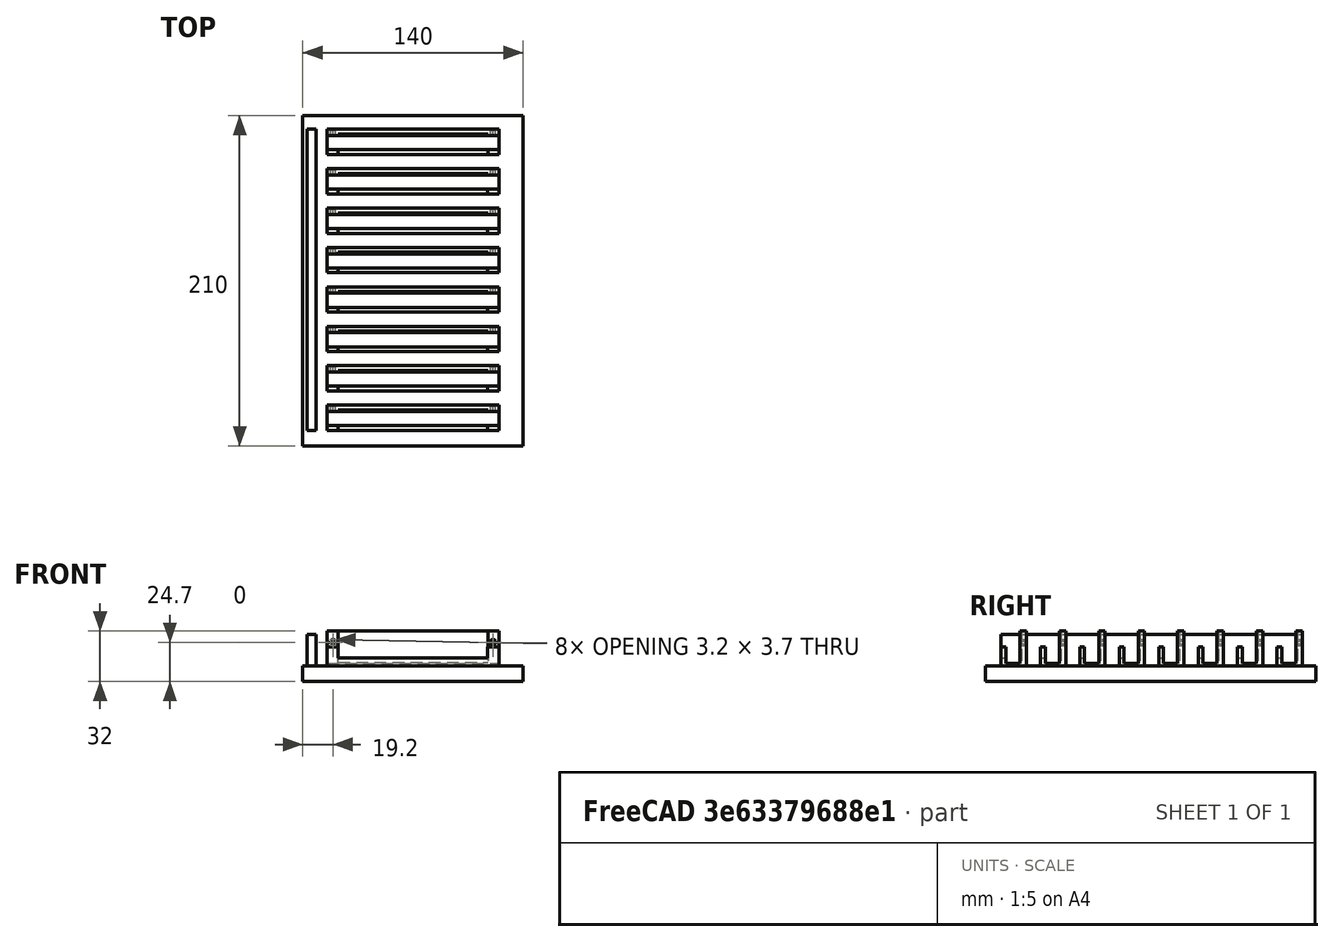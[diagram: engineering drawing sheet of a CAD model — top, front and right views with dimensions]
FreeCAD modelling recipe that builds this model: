
FCSTD DOCUMENT  (FreeCAD 1.0R39109 (Git))
Label: parking
License: All rights reserved
LicenseURL: http://en.wikipedia.org/wiki/All_rights_reserved
objects: Sketcher::SketchObject×20, PartDesign::Pocket×17, PartDesign::Plane×8, Mesh::Feature×6, PartDesign::Pad×3, Spreadsheet::Sheet×1, PartDesign::Body×1
note: 109 computed .brp shape members not serialized (recipe doc carries the construction recipe); baked Part::Feature solids carry a one-line shape summary decoded from their .brp

FEATURE [Sketcher::SketchObject] Sketch
  ArcFitTolerance = 0
  AttachmentSupport = -> [XY_Plane]
  FullyConstrained = true
  MakeInternals = false
  MapMode = 5
  sketch-geometry (4):
    g0: LineSegment StartX=-70 StartY=100 StartZ=0 EndX=70 EndY=100 EndZ=0
    g1: LineSegment StartX=70 StartY=100 StartZ=0 EndX=70 EndY=-110 EndZ=0
    g2: LineSegment StartX=70 StartY=-110 StartZ=0 EndX=-70 EndY=-110 EndZ=0
    g3: LineSegment StartX=-70 StartY=-110 StartZ=0 EndX=-70 EndY=100 EndZ=0
  constraints (11):
    c: Coincident(g0,g1)
    c: Coincident(g1,g2)
    c: Coincident(g2,g3)
    c: Coincident(g3,g0)
    c: Horizontal(g2)
    c: Vertical(g1)
    c: Symmetric(g0,g0,g-2)
    c: DistanceY(g2,g0) = 210
    c: DistanceX(g0,g0) = 140
    c: DistanceY(g-1,g0) = 100
    c: Vertical(g3)
FEATURE [PartDesign::Pad] Pad
  Direction = (0,0,1)
  Length = 12
  Length2 = -2
  Profile = -> Sketch
  ReferenceAxis = -> Sketch [N_Axis]
  Reversed = true
  Suppressed = false
  Type = 4
FEATURE [Spreadsheet::Sheet] Spreadsheet001  label="data001"
  cells = A1='tolerance; B1(tolerance)=0.25; A2='cradle_width; B2(cradle_width)=109.2; A3='cradle_height; B3(cradle_height)=20; A4='cradle_holdermag_sep; B4(cradle_holdermag_sep)=101.6; A5='cradle_holdermag_height; B5(cradle_holdermag_height)=12.7; A6='cradle_thick; B6(cradle_thick)=5; A7='cradlebase_height; B7(cradlebase_height)=7; A8='cradlebase_depth; B8(cradlebase_depth)=20; A9='cradlebase_frontdepth; B9(cradlebase_frontdepth)=10; A10='cradle_holdermag_dim1; B10(cradle_holdermag_dim1)=3; A11='cradle_holdermag_dim2; B11(cradle_holdermag_dim2)=3
FEATURE [Sketcher::SketchObject] Sketch001
  ArcFitTolerance = 0
  AttachmentSupport = -> [YZ_Plane]
  FullyConstrained = true
  MakeInternals = false
  MapMode = 5
  Placement = pos=(0,0,0) rot=(0.57735,0.57735,0.57735;2.0944rad)
  expr: Constraints[10] = <<data001>>.cradle_height
  sketch-geometry (112):
    g0: ArcOfCircle CenterX=-88 CenterY=-6e-16 CenterZ=0 NormalX=0 NormalY=0 NormalZ=1 AngleXU=0 Radius=12 StartAngle=3.14159 EndAngle=4.71239
    g1: LineSegment [constr] StartX=-100 StartY=9e-16 StartZ=0 EndX=-88 EndY=-6e-16 EndZ=0
    g2: LineSegment StartX=-88 StartY=-6e-16 StartZ=0 EndX=-88 EndY=20 EndZ=0
    g3: LineSegment StartX=-88 StartY=20 StartZ=0 EndX=-84 EndY=20 EndZ=0
    g4: LineSegment StartX=-84 StartY=20 StartZ=0 EndX=-84 EndY=-12 EndZ=0
    g5: LineSegment StartX=-88 StartY=-12 StartZ=0 EndX=-84 EndY=-12 EndZ=0
    g6: LineSegment [constr] StartX=-88 StartY=-6e-16 StartZ=0 EndX=-88 EndY=-12 EndZ=0
    g7: LineSegment StartX=-88 StartY=-6e-16 StartZ=0 EndX=-88 EndY=-0.5 EndZ=0
    g8: LineSegment StartX=-88 StartY=-0.5 StartZ=0 EndX=-97 EndY=-0.5 EndZ=0
    g9: LineSegment StartX=-97 StartY=-0.5 StartZ=0 EndX=-97 EndY=0 EndZ=0
    g10: LineSegment StartX=-100 StartY=9e-16 StartZ=0 EndX=-100 EndY=10 EndZ=0
    g11: LineSegment StartX=-100 StartY=10 StartZ=0 EndX=-97 EndY=10 EndZ=0
    g12: LineSegment StartX=-97 StartY=10 StartZ=0 EndX=-97 EndY=0 EndZ=0
    g13: LineSegment [constr] StartX=-100 StartY=10 StartZ=0 EndX=100 EndY=10 EndZ=0
    g14: ArcOfCircle CenterX=-62.9683 CenterY=2e-15 CenterZ=0 NormalX=0 NormalY=0 NormalZ=1 AngleXU=0 Radius=12 StartAngle=3.14159 EndAngle=4.71239
    g15: LineSegment [constr] StartX=-74.9683 StartY=0 StartZ=0 EndX=-62.9683 EndY=2e-15 EndZ=0
    g16: LineSegment StartX=-62.9683 StartY=2e-15 StartZ=0 EndX=-62.9683 EndY=20 EndZ=0
    g17: LineSegment StartX=-62.9683 StartY=20 StartZ=0 EndX=-58.9683 EndY=20 EndZ=0
    g18: LineSegment StartX=-58.9683 StartY=20 StartZ=0 EndX=-58.9683 EndY=-12 EndZ=0
    g19: LineSegment StartX=-62.9683 StartY=-12 StartZ=0 EndX=-58.9683 EndY=-12 EndZ=0
    g20: LineSegment [constr] StartX=-62.9683 StartY=2e-15 StartZ=0 EndX=-62.9683 EndY=-12 EndZ=0
    g21: LineSegment StartX=-62.9683 StartY=2e-15 StartZ=0 EndX=-62.9683 EndY=-0.5 EndZ=0
    g22: LineSegment StartX=-62.9683 StartY=-0.5 StartZ=0 EndX=-71.9683 EndY=-0.5 EndZ=0
    g23: LineSegment StartX=-71.9683 StartY=-0.5 StartZ=0 EndX=-71.9683 EndY=0 EndZ=0
    g24: LineSegment StartX=-74.9683 StartY=0 StartZ=0 EndX=-74.9683 EndY=10 EndZ=0
    g25: LineSegment StartX=-74.9683 StartY=10 StartZ=0 EndX=-71.9683 EndY=10 EndZ=0
    g26: LineSegment StartX=-71.9683 StartY=10 StartZ=0 EndX=-71.9683 EndY=0 EndZ=0
    g27: LineSegment [constr] StartX=-100 StartY=9e-16 StartZ=0 EndX=-74.9683 EndY=0 EndZ=0
    g28: ArcOfCircle CenterX=-37.9367 CenterY=2.1e-15 CenterZ=0 NormalX=0 NormalY=0 NormalZ=1 AngleXU=0 Radius=12 StartAngle=3.14159 EndAngle=4.71239
    g29: LineSegment [constr] StartX=-49.9367 StartY=-1.8e-15 StartZ=0 EndX=-37.9367 EndY=2.1e-15 EndZ=0
    g30: LineSegment StartX=-37.9367 StartY=2.1e-15 StartZ=0 EndX=-37.9367 EndY=20 EndZ=0
    g31: LineSegment StartX=-37.9367 StartY=20 StartZ=0 EndX=-33.9367 EndY=20 EndZ=0
    g32: LineSegment StartX=-33.9367 StartY=20 StartZ=0 EndX=-33.9367 EndY=-12 EndZ=0
    g33: LineSegment StartX=-37.9367 StartY=-12 StartZ=0 EndX=-33.9367 EndY=-12 EndZ=0
    g34: LineSegment [constr] StartX=-37.9367 StartY=2.1e-15 StartZ=0 EndX=-37.9367 EndY=-12 EndZ=0
    g35: LineSegment StartX=-37.9367 StartY=2.1e-15 StartZ=0 EndX=-37.9367 EndY=-0.5 EndZ=0
    g36: LineSegment StartX=-37.9367 StartY=-0.5 StartZ=0 EndX=-46.9367 EndY=-0.5 EndZ=0
    g37: LineSegment StartX=-46.9367 StartY=-0.5 StartZ=0 EndX=-46.9367 EndY=0 EndZ=0
    g38: LineSegment StartX=-49.9367 StartY=-1.8e-15 StartZ=0 EndX=-49.9367 EndY=10 EndZ=0
    g39: LineSegment StartX=-49.9367 StartY=10 StartZ=0 EndX=-46.9367 EndY=10 EndZ=0
    g40: LineSegment StartX=-46.9367 StartY=10 StartZ=0 EndX=-46.9367 EndY=0 EndZ=0
    g41: LineSegment [constr] StartX=-74.9683 StartY=0 StartZ=0 EndX=-49.9367 EndY=-1.8e-15 EndZ=0
    g42: ArcOfCircle CenterX=-12.905 CenterY=2.1e-15 CenterZ=0 NormalX=0 NormalY=0 NormalZ=1 AngleXU=0 Radius=12 StartAngle=3.14159 EndAngle=4.71239
    g43: LineSegment [constr] StartX=-24.905 StartY=-1.8e-15 StartZ=0 EndX=-12.905 EndY=2.1e-15 EndZ=0
    g44: LineSegment StartX=-12.905 StartY=2.1e-15 StartZ=0 EndX=-12.905 EndY=20 EndZ=0
    g45: LineSegment StartX=-12.905 StartY=20 StartZ=0 EndX=-8.90501 EndY=20 EndZ=0
    g46: LineSegment StartX=-8.90501 StartY=20 StartZ=0 EndX=-8.90501 EndY=-12 EndZ=0
    g47: LineSegment StartX=-12.905 StartY=-12 StartZ=0 EndX=-8.90501 EndY=-12 EndZ=0
    g48: LineSegment [constr] StartX=-12.905 StartY=2.1e-15 StartZ=0 EndX=-12.905 EndY=-12 EndZ=0
    g49: LineSegment StartX=-12.905 StartY=2.1e-15 StartZ=0 EndX=-12.905 EndY=-0.5 EndZ=0
    g50: LineSegment StartX=-12.905 StartY=-0.5 StartZ=0 EndX=-21.905 EndY=-0.5 EndZ=0
    g51: LineSegment StartX=-21.905 StartY=-0.5 StartZ=0 EndX=-21.905 EndY=0 EndZ=0
    g52: LineSegment StartX=-24.905 StartY=-1.8e-15 StartZ=0 EndX=-24.905 EndY=10 EndZ=0
    g53: LineSegment StartX=-24.905 StartY=10 StartZ=0 EndX=-21.905 EndY=10 EndZ=0
    g54: LineSegment StartX=-21.905 StartY=10 StartZ=0 EndX=-21.905 EndY=0 EndZ=0
    g55: LineSegment [constr] StartX=-49.9367 StartY=-1.8e-15 StartZ=0 EndX=-24.905 EndY=-1.8e-15 EndZ=0
    g56: ArcOfCircle CenterX=12.1266 CenterY=1.4e-15 CenterZ=0 NormalX=0 NormalY=0 NormalZ=1 AngleXU=0 Radius=12 StartAngle=3.14159 EndAngle=4.71239
    g57: LineSegment [constr] StartX=0.126648 StartY=-2.5e-15 StartZ=0 EndX=12.1266 EndY=1.4e-15 EndZ=0
    g58: LineSegment StartX=12.1266 StartY=1.4e-15 StartZ=0 EndX=12.1266 EndY=20 EndZ=0
    g59: LineSegment StartX=12.1266 StartY=20 StartZ=0 EndX=16.1266 EndY=20 EndZ=0
    g60: LineSegment StartX=16.1266 StartY=20 StartZ=0 EndX=16.1266 EndY=-12 EndZ=0
    g61: LineSegment StartX=12.1266 StartY=-12 StartZ=0 EndX=16.1266 EndY=-12 EndZ=0
    g62: LineSegment [constr] StartX=12.1266 StartY=1.4e-15 StartZ=0 EndX=12.1266 EndY=-12 EndZ=0
    g63: LineSegment StartX=12.1266 StartY=1.4e-15 StartZ=0 EndX=12.1266 EndY=-0.5 EndZ=0
    g64: LineSegment StartX=12.1266 StartY=-0.5 StartZ=0 EndX=3.12665 EndY=-0.5 EndZ=0
    g65: LineSegment StartX=3.12665 StartY=-0.5 StartZ=0 EndX=3.12665 EndY=0 EndZ=0
    g66: LineSegment StartX=0.126648 StartY=-2.5e-15 StartZ=0 EndX=0.126648 EndY=10 EndZ=0
    g67: LineSegment StartX=0.126648 StartY=10 StartZ=0 EndX=3.12665 EndY=10 EndZ=0
    g68: LineSegment StartX=3.12665 StartY=10 StartZ=0 EndX=3.12665 EndY=0 EndZ=0
    g69: LineSegment [constr] StartX=-24.905 StartY=-1.8e-15 StartZ=0 EndX=0.126648 EndY=-2.5e-15 EndZ=0
    g70: ArcOfCircle CenterX=37.1583 CenterY=-2.4e-15 CenterZ=0 NormalX=0 NormalY=0 NormalZ=1 AngleXU=0 Radius=12 StartAngle=3.14159 EndAngle=4.71239
    g71: LineSegment [constr] StartX=25.1583 StartY=0 StartZ=0 EndX=37.1583 EndY=-2.4e-15 EndZ=0
    g72: LineSegment StartX=37.1583 StartY=-2.4e-15 StartZ=0 EndX=37.1583 EndY=20 EndZ=0
    g73: LineSegment StartX=37.1583 StartY=20 StartZ=0 EndX=41.1583 EndY=20 EndZ=0
    g74: LineSegment StartX=41.1583 StartY=20 StartZ=0 EndX=41.1583 EndY=-12 EndZ=0
    g75: LineSegment StartX=37.1583 StartY=-12 StartZ=0 EndX=41.1583 EndY=-12 EndZ=0
    g76: LineSegment [constr] StartX=37.1583 StartY=-2.4e-15 StartZ=0 EndX=37.1583 EndY=-12 EndZ=0
    g77: LineSegment StartX=37.1583 StartY=-2.4e-15 StartZ=0 EndX=37.1583 EndY=-0.5 EndZ=0
    g78: LineSegment StartX=37.1583 StartY=-0.5 StartZ=0 EndX=28.1583 EndY=-0.5 EndZ=0
    g79: LineSegment StartX=28.1583 StartY=-0.5 StartZ=0 EndX=28.1583 EndY=0 EndZ=0
    g80: LineSegment StartX=25.1583 StartY=0 StartZ=0 EndX=25.1583 EndY=10 EndZ=0
    g81: LineSegment StartX=25.1583 StartY=10 StartZ=0 EndX=28.1583 EndY=10 EndZ=0
    g82: LineSegment StartX=28.1583 StartY=10 StartZ=0 EndX=28.1583 EndY=0 EndZ=0
    g83: LineSegment [constr] StartX=0.126648 StartY=-2.5e-15 StartZ=0 EndX=25.1583 EndY=0 EndZ=0
    g84: ArcOfCircle CenterX=62.19 CenterY=1.7e-15 CenterZ=0 NormalX=0 NormalY=0 NormalZ=1 AngleXU=0 Radius=12 StartAngle=3.14159 EndAngle=4.71239
    g85: LineSegment [constr] StartX=50.19 StartY=0 StartZ=0 EndX=62.19 EndY=1.7e-15 EndZ=0
    g86: LineSegment StartX=62.19 StartY=1.7e-15 StartZ=0 EndX=62.19 EndY=20 EndZ=0
    g87: LineSegment StartX=62.19 StartY=20 StartZ=0 EndX=66.19 EndY=20 EndZ=0
    g88: LineSegment StartX=66.19 StartY=20 StartZ=0 EndX=66.19 EndY=-12 EndZ=0
    g89: LineSegment StartX=62.19 StartY=-12 StartZ=0 EndX=66.19 EndY=-12 EndZ=0
    g90: LineSegment [constr] StartX=62.19 StartY=1.7e-15 StartZ=0 EndX=62.19 EndY=-12 EndZ=0
    g91: LineSegment StartX=62.19 StartY=1.7e-15 StartZ=0 EndX=62.19 EndY=-0.5 EndZ=0
    g92: LineSegment StartX=62.19 StartY=-0.5 StartZ=0 EndX=53.19 EndY=-0.5 EndZ=0
    g93: LineSegment StartX=53.19 StartY=-0.5 StartZ=0 EndX=53.19 EndY=0 EndZ=0
    g94: LineSegment StartX=50.19 StartY=0 StartZ=0 EndX=50.19 EndY=10 EndZ=0
    g95: LineSegment StartX=50.19 StartY=10 StartZ=0 EndX=53.19 EndY=10 EndZ=0
    g96: LineSegment StartX=53.19 StartY=10 StartZ=0 EndX=53.19 EndY=0 EndZ=0
    g97: LineSegment [constr] StartX=25.1583 StartY=0 StartZ=0 EndX=50.19 EndY=0 EndZ=0
    g98: ArcOfCircle CenterX=87.2216 CenterY=-6e-16 CenterZ=0 NormalX=0 NormalY=0 NormalZ=1 AngleXU=0 Radius=12 StartAngle=3.14159 EndAngle=4.71239
    g99: LineSegment [constr] StartX=75.2216 StartY=0 StartZ=0 EndX=87.2216 EndY=-6e-16 EndZ=0
    g100: LineSegment StartX=87.2216 StartY=-6e-16 StartZ=0 EndX=87.2216 EndY=20 EndZ=0
    g101: LineSegment StartX=87.2216 StartY=20 StartZ=0 EndX=91.2216 EndY=20 EndZ=0
    g102: LineSegment StartX=91.2216 StartY=20 StartZ=0 EndX=91.2216 EndY=-12 EndZ=0
    g103: LineSegment StartX=87.2216 StartY=-12 StartZ=0 EndX=91.2216 EndY=-12 EndZ=0
    g104: LineSegment [constr] StartX=87.2216 StartY=-6e-16 StartZ=0 EndX=87.2216 EndY=-12 EndZ=0
    g105: LineSegment StartX=87.2216 StartY=-6e-16 StartZ=0 EndX=87.2216 EndY=-0.5 EndZ=0
    g106: LineSegment StartX=87.2216 StartY=-0.5 StartZ=0 EndX=78.2216 EndY=-0.5 EndZ=0
    g107: LineSegment StartX=78.2216 StartY=-0.5 StartZ=0 EndX=78.2216 EndY=0 EndZ=0
    g108: LineSegment StartX=75.2216 StartY=0 StartZ=0 EndX=75.2216 EndY=10 EndZ=0
    g109: LineSegment StartX=75.2216 StartY=10 StartZ=0 EndX=78.2216 EndY=10 EndZ=0
    g110: LineSegment StartX=78.2216 StartY=10 StartZ=0 EndX=78.2216 EndY=0 EndZ=0
    g111: LineSegment [constr] StartX=50.19 StartY=0 StartZ=0 EndX=75.2216 EndY=0 EndZ=0
  constraints (313):
    c: Radius(g0) = 12
    c: Coincident(g1,g0)
    c: Coincident(g1,g0)
    c: Coincident(g2,g0)
    c: Coincident(g3,g2)
    c: Horizontal(g3)
    c: Coincident(g5,g0)
    c: Coincident(g5,g4)
    c: Horizontal(g5)
    c: Vertical(g4)
    c: Distance(g2,g0) = 20
    c: Coincident(g4,g3)
    c: Coincident(g6,g0)
    c: Coincident(g6,g0)
    c: Angle(g1,g6) = 1.5708
    c: Angle(g2,g1) = 1.5708
    c: DistanceX(g2,g3) = 4
    c: Coincident(g7,g0)
    c: PointOnObject(g7,g6)
    c: Coincident(g8,g7)
    c: Coincident(g9,g8)
    c: PointOnObject(g9,g1)
    c: Distance(g7,g0) = 0.5
    c: Parallel(g9,g6)
    c: Parallel(g8,g1)
    c: Distance(g8,g7) = 9
    c: Coincident(g10,g0)
    c: Coincident(g11,g10)
    c: Coincident(g12,g11)
    c: Coincident(g12,g9)
    c: Parallel(g10,g2)
    c: Parallel(g6,g4)
    c: Parallel(g10,g12)
    c: Parallel(g11,g1)
    c: PointOnObject(g0,g-1)
    c: Distance(g10) = 10
    c: Distance(g0,g-1) = 100
    c: Coincident(g13,g10)
    c: Horizontal(g13)
    c: DistanceX(g13,g13) = 200
    c: Equal(g0,g14) = 12
    c: Coincident(g15,g14)
    c: Coincident(g15,g14)
    c: Coincident(g16,g14)
    c: Coincident(g17,g16)
    c: Horizontal(g17)
    c: Coincident(g19,g14)
    c: Coincident(g19,g18)
    c: Horizontal(g19)
    c: Vertical(g18)
    c: Distance(g16,g14) = 20
    c: Coincident(g18,g17)
    c: Coincident(g20,g14)
    c: Coincident(g20,g14)
    c: Angle(g15,g20) = 1.5708
    c: Angle(g16,g15) = 1.5708
    c: DistanceX(g16,g17) = 4
    c: Coincident(g21,g14)
    c: PointOnObject(g21,g20)
    c: Coincident(g22,g21)
    c: Coincident(g23,g22)
    c: PointOnObject(g23,g15)
    c: Distance(g21,g14) = 0.5
    c: Parallel(g23,g20)
    c: Parallel(g22,g15)
    c: Distance(g22,g21) = 9
    c: Coincident(g24,g14)
    c: Coincident(g25,g24)
    c: Coincident(g26,g25)
    c: Coincident(g26,g23)
    c: Parallel(g24,g16)
    c: Parallel(g20,g18)
    c: Parallel(g24,g26)
    c: Parallel(g25,g15)
    c: Equal(g10,g24) = 10
    c: Coincident(g0,g27)
    c: Coincident(g14,g27)
    c: Distance(g27) = 25.0317
    c: Angle(g27) = 0
    c: Equal(g0,g28) = 12
    c: Coincident(g29,g28)
    c: Coincident(g29,g28)
    c: Coincident(g30,g28)
    c: Coincident(g31,g30)
    c: Horizontal(g31)
    c: Coincident(g33,g28)
    c: Coincident(g33,g32)
    c: Horizontal(g33)
    c: Vertical(g32)
    c: Distance(g30,g28) = 20
    c: Coincident(g32,g31)
    c: Coincident(g34,g28)
    c: Coincident(g34,g28)
    c: Angle(g29,g34) = 1.5708
    c: Angle(g30,g29) = 1.5708
    c: DistanceX(g30,g31) = 4
    c: Coincident(g35,g28)
    c: PointOnObject(g35,g34)
    c: Coincident(g36,g35)
    c: Coincident(g37,g36)
    c: PointOnObject(g37,g29)
    c: Distance(g35,g28) = 0.5
    c: Parallel(g37,g34)
    c: Parallel(g36,g29)
    c: Distance(g36,g35) = 9
    c: Coincident(g38,g28)
    c: Coincident(g39,g38)
    c: Coincident(g40,g39)
    c: Coincident(g40,g37)
    c: Parallel(g38,g30)
    c: Parallel(g34,g32)
    c: Parallel(g38,g40)
    c: Parallel(g39,g29)
    c: Equal(g10,g38) = 10
    c: Coincident(g14,g41)
    c: Coincident(g28,g41)
    c: Equal(g27,g41)
    c: Parallel(g41,g27)
    c: Equal(g0,g42) = 12
    c: Coincident(g43,g42)
    c: Coincident(g43,g42)
    c: Coincident(g44,g42)
    c: Coincident(g45,g44)
    c: Horizontal(g45)
    c: Coincident(g47,g42)
    c: Coincident(g47,g46)
    c: Horizontal(g47)
    c: Vertical(g46)
    c: Distance(g44,g42) = 20
    c: Coincident(g46,g45)
    c: Coincident(g48,g42)
    c: Coincident(g48,g42)
    c: Angle(g43,g48) = 1.5708
    c: Angle(g44,g43) = 1.5708
    c: DistanceX(g44,g45) = 4
    c: Coincident(g49,g42)
    c: PointOnObject(g49,g48)
    c: Coincident(g50,g49)
    c: Coincident(g51,g50)
    c: PointOnObject(g51,g43)
    c: Distance(g49,g42) = 0.5
    c: Parallel(g51,g48)
    c: Parallel(g50,g43)
    c: Distance(g50,g49) = 9
    c: Coincident(g52,g42)
    c: Coincident(g53,g52)
    c: Coincident(g54,g53)
    c: Coincident(g54,g51)
    c: Parallel(g52,g44)
    c: Parallel(g48,g46)
    c: Parallel(g52,g54)
    c: Parallel(g53,g43)
    c: Equal(g10,g52) = 10
    c: Coincident(g28,g55)
    c: Coincident(g42,g55)
    c: Equal(g27,g55)
    c: Parallel(g55,g27)
    c: Equal(g0,g56) = 12
    c: Coincident(g57,g56)
    c: Coincident(g57,g56)
    c: Coincident(g58,g56)
    c: Coincident(g59,g58)
    c: Horizontal(g59)
    c: Coincident(g61,g56)
    c: Coincident(g61,g60)
    c: Horizontal(g61)
    c: Vertical(g60)
    c: Distance(g58,g56) = 20
    c: Coincident(g60,g59)
    c: Coincident(g62,g56)
    c: Coincident(g62,g56)
    c: Angle(g57,g62) = 1.5708
    c: Angle(g58,g57) = 1.5708
    c: DistanceX(g58,g59) = 4
    c: Coincident(g63,g56)
    c: PointOnObject(g63,g62)
    c: Coincident(g64,g63)
    c: Coincident(g65,g64)
    c: PointOnObject(g65,g57)
    c: Distance(g63,g56) = 0.5
    c: Parallel(g65,g62)
    c: Parallel(g64,g57)
    c: Distance(g64,g63) = 9
    c: Coincident(g66,g56)
    c: Coincident(g67,g66)
    c: Coincident(g68,g67)
    c: Coincident(g68,g65)
    c: Parallel(g66,g58)
    c: Parallel(g62,g60)
    c: Parallel(g66,g68)
    c: Parallel(g67,g57)
    c: Equal(g10,g66) = 10
    c: Coincident(g42,g69)
    c: Coincident(g56,g69)
    c: Equal(g27,g69)
    c: Parallel(g69,g27)
    c: Equal(g0,g70) = 12
    c: Coincident(g71,g70)
    c: Coincident(g71,g70)
    c: Coincident(g72,g70)
    c: Coincident(g73,g72)
    c: Horizontal(g73)
    c: Coincident(g75,g70)
    c: Coincident(g75,g74)
    c: Horizontal(g75)
    c: Vertical(g74)
    c: Distance(g72,g70) = 20
    c: Coincident(g74,g73)
    c: Coincident(g76,g70)
    c: Coincident(g76,g70)
    c: Angle(g71,g76) = 1.5708
    c: Angle(g72,g71) = 1.5708
    c: DistanceX(g72,g73) = 4
    c: Coincident(g77,g70)
    c: PointOnObject(g77,g76)
    c: Coincident(g78,g77)
    c: Coincident(g79,g78)
    c: PointOnObject(g79,g71)
    c: Distance(g77,g70) = 0.5
    c: Parallel(g79,g76)
    c: Parallel(g78,g71)
    c: Distance(g78,g77) = 9
    c: Coincident(g80,g70)
    c: Coincident(g81,g80)
    c: Coincident(g82,g81)
    c: Coincident(g82,g79)
    c: Parallel(g80,g72)
    c: Parallel(g76,g74)
    c: Parallel(g80,g82)
    c: Parallel(g81,g71)
    c: Equal(g10,g80) = 10
    c: Coincident(g56,g83)
    c: Coincident(g70,g83)
    c: Equal(g27,g83)
    c: Parallel(g83,g27)
    c: Equal(g0,g84) = 12
    c: Coincident(g85,g84)
    c: Coincident(g85,g84)
    c: Coincident(g86,g84)
    c: Coincident(g87,g86)
    c: Horizontal(g87)
    c: Coincident(g89,g84)
    c: Coincident(g89,g88)
    c: Horizontal(g89)
    c: Vertical(g88)
    c: Distance(g86,g84) = 20
    c: Coincident(g88,g87)
    c: Coincident(g90,g84)
    c: Coincident(g90,g84)
    c: Angle(g85,g90) = 1.5708
    c: Angle(g86,g85) = 1.5708
    c: DistanceX(g86,g87) = 4
    c: Coincident(g91,g84)
    c: PointOnObject(g91,g90)
    c: Coincident(g92,g91)
    c: Coincident(g93,g92)
    c: PointOnObject(g93,g85)
    c: Distance(g91,g84) = 0.5
    c: Parallel(g93,g90)
    c: Parallel(g92,g85)
    c: Distance(g92,g91) = 9
    c: Coincident(g94,g84)
    c: Coincident(g95,g94)
    c: Coincident(g96,g95)
    c: Coincident(g96,g93)
    c: Parallel(g94,g86)
    c: Parallel(g90,g88)
    c: Parallel(g94,g96)
    c: Parallel(g95,g85)
    c: Equal(g10,g94) = 10
    c: Coincident(g70,g97)
    c: Coincident(g84,g97)
    c: Equal(g27,g97)
    c: Parallel(g97,g27)
    c: Equal(g0,g98) = 12
    c: Coincident(g99,g98)
    c: Coincident(g99,g98)
    c: Coincident(g100,g98)
    c: Coincident(g101,g100)
    c: Horizontal(g101)
    c: Coincident(g103,g98)
    c: Coincident(g103,g102)
    c: Horizontal(g103)
    c: Vertical(g102)
    c: Distance(g100,g98) = 20
    c: Coincident(g102,g101)
    c: Coincident(g104,g98)
    c: Coincident(g104,g98)
    c: Angle(g99,g104) = 1.5708
    c: Angle(g100,g99) = 1.5708
    c: DistanceX(g100,g101) = 4
    c: Coincident(g105,g98)
    c: PointOnObject(g105,g104)
    c: Coincident(g106,g105)
    c: Coincident(g107,g106)
    c: PointOnObject(g107,g99)
    c: Distance(g105,g98) = 0.5
    c: Parallel(g107,g104)
    c: Parallel(g106,g99)
    c: Distance(g106,g105) = 9
    c: Coincident(g108,g98)
    c: Coincident(g109,g108)
    c: Coincident(g110,g109)
    c: Coincident(g110,g107)
    c: Parallel(g108,g100)
    c: Parallel(g104,g102)
    c: Parallel(g108,g110)
    c: Parallel(g109,g99)
    c: Equal(g10,g108) = 10
    c: Coincident(g84,g111)
    c: Coincident(g98,g111)
    c: Equal(g27,g111)
    c: Parallel(g111,g27)
FEATURE [PartDesign::Pad] Pad001
  BaseFeature = -> Pad
  Direction = (1,0,0)
  Length = 109.2
  Length2 = 10
  Midplane = true
  Profile = -> Sketch001
  ReferenceAxis = -> Sketch001 [N_Axis]
  Suppressed = false
  Type = 0
  expr: Length = <<data001>>.cradle_width
FEATURE [Mesh::Feature] Mesh  label="20 degrees"
FEATURE [Mesh::Feature] Mesh001  label="30 degrees"
FEATURE [Mesh::Feature] Mesh002  label="5 degrees"
FEATURE [Mesh::Feature] Mesh003  label="0 degrees"
FEATURE [Mesh::Feature] Mesh004  label="Pocket008 (Meshed)"
FEATURE [Sketcher::SketchObject] Sketch002
  ArcFitTolerance = 0
  AttachmentSupport = -> [Pad001]
  FullyConstrained = false
  MakeInternals = false
  MapMode = 5
  Placement = pos=(0,0,-2) rot=(0,0,1;0rad)
  sketch-geometry (4):
    g0: LineSegment StartX=-67.1563 StartY=-100.063 StartZ=0 EndX=-61.6543 EndY=-100.063 EndZ=0
    g1: LineSegment StartX=-61.6543 StartY=-100.063 StartZ=0 EndX=-61.6543 EndY=91.28 EndZ=0
    g2: LineSegment StartX=-61.6543 StartY=91.28 StartZ=0 EndX=-67.1563 EndY=91.28 EndZ=0
    g3: LineSegment StartX=-67.1563 StartY=91.28 StartZ=0 EndX=-67.1563 EndY=-100.063 EndZ=0
  constraints (8):
    c: Coincident(g0,g1)
    c: Coincident(g1,g2)
    c: Coincident(g2,g3)
    c: Coincident(g3,g0)
    c: Horizontal(g0)
    c: Horizontal(g2)
    c: Vertical(g1)
    c: Vertical(g3)
FEATURE [PartDesign::Pad] Pad002
  BaseFeature = -> Pad001
  Direction = (0,0,1)
  Length = 20
  Length2 = 10
  Profile = -> Sketch002
  ReferenceAxis = -> Sketch002 [N_Axis]
  Suppressed = false
  Type = 0
FEATURE [PartDesign::Plane] DatumPlane
  AttachmentSupport = -> [Pad002]
  Length = 156.733
  MapMode = 5
  Placement = pos=(0,-88,0) rot=(1,0,0;1.5708rad)
  ResizeMode = 0
  Width = 66.7332
FEATURE [Sketcher::SketchObject] Sketch004
  ArcFitTolerance = 0
  AttachmentSupport = -> [DatumPlane]
  FullyConstrained = true
  MakeInternals = false
  MapMode = 5
  Placement = pos=(0,-88,0) rot=(1,0,0;1.5708rad)
  expr: Constraints[38] = <<data001>>.cradle_holdermag_sep
  sketch-geometry (14):
    g0: LineSegment StartX=-49.1979 StartY=11.775 StartZ=0 EndX=-49.1979 EndY=13.625 EndZ=0
    g1: LineSegment StartX=-49.1979 StartY=13.625 StartZ=0 EndX=-50.8 EndY=14.55 EndZ=0
    g2: LineSegment StartX=-50.8 StartY=14.55 StartZ=0 EndX=-52.4021 EndY=13.625 EndZ=0
    g3: LineSegment StartX=-52.4021 StartY=13.625 StartZ=0 EndX=-52.4021 EndY=11.775 EndZ=0
    g4: LineSegment StartX=-52.4021 StartY=11.775 StartZ=0 EndX=-50.8 EndY=10.85 EndZ=0
    g5: LineSegment StartX=-50.8 StartY=10.85 StartZ=0 EndX=-49.1979 EndY=11.775 EndZ=0
    g6: Circle [constr] CenterX=-50.8 CenterY=12.7 CenterZ=0 NormalX=0 NormalY=0 NormalZ=1 AngleXU=0 Radius=1.85
    g7: LineSegment StartX=52.4021 StartY=11.775 StartZ=0 EndX=52.4021 EndY=13.625 EndZ=0
    g8: LineSegment StartX=52.4021 StartY=13.625 StartZ=0 EndX=50.8 EndY=14.55 EndZ=0
    g9: LineSegment StartX=50.8 StartY=14.55 StartZ=0 EndX=49.1979 EndY=13.625 EndZ=0
    g10: LineSegment StartX=49.1979 StartY=13.625 StartZ=0 EndX=49.1979 EndY=11.775 EndZ=0
    g11: LineSegment StartX=49.1979 StartY=11.775 StartZ=0 EndX=50.8 EndY=10.85 EndZ=0
    g12: LineSegment StartX=50.8 StartY=10.85 StartZ=0 EndX=52.4021 EndY=11.775 EndZ=0
    g13: Circle [constr] CenterX=50.8 CenterY=12.7 CenterZ=0 NormalX=0 NormalY=0 NormalZ=1 AngleXU=0 Radius=1.85
  constraints (33):
    c: Coincident(g0,g1)
    c: Coincident(g1,g2)
    c: Coincident(g2,g3)
    c: Coincident(g3,g4)
    c: Coincident(g4,g5)
    c: Coincident(g5,g0)
    c: Equal(g0, g1-g5) x5
    c: PointOnObject(g0,g6)
    c: PointOnObject(g1,g6)
    c: PointOnObject(g2,g6)
    c: PointOnObject(g3,g6)
    c: PointOnObject(g4,g6)
    c: PointOnObject(g5,g6)
    c: Coincident(g7,g8)
    c: Coincident(g8,g9)
    c: Coincident(g9,g10)
    c: Coincident(g10,g11)
    c: Coincident(g11,g12)
    c: Coincident(g12,g7)
    c: Equal(g7, g8-g12) x5
    c: PointOnObject(g7,g13)
    c: PointOnObject(g8,g13)
    c: PointOnObject(g9,g13)
    c: PointOnObject(g10,g13)
    c: PointOnObject(g11,g13)
    c: PointOnObject(g12,g13)
    c: Parallel(g0,g-2)
    c: Equal(g2,g10)
    c: Parallel(g10,g-2)
    c: Symmetric(g6,g13,g-2)
    c: DistanceX(g6,g13) = 101.6
    c: DistanceY(g-1,g6) = 12.7
    c: Radius(g6) = 1.85
FEATURE [Sketcher::SketchObject] Sketch005
  ArcFitTolerance = 0
  AttachmentSupport = -> [DatumPlane]
  FullyConstrained = true
  MakeInternals = false
  MapMode = 5
  Placement = pos=(0,-88,0) rot=(1,0,0;1.5708rad)
  sketch-geometry (4):
    g0: LineSegment StartX=-47.5 StartY=22 StartZ=0 EndX=47.5 EndY=22 EndZ=0
    g1: LineSegment StartX=47.5 StartY=22 StartZ=0 EndX=47.5 EndY=0 EndZ=0
    g2: LineSegment StartX=47.5 StartY=0 StartZ=0 EndX=-47.5 EndY=0 EndZ=0
    g3: LineSegment StartX=-47.5 StartY=0 StartZ=0 EndX=-47.5 EndY=22 EndZ=0
  constraints (11):
    c: Coincident(g0,g1)
    c: Coincident(g1,g2)
    c: Coincident(g2,g3)
    c: Coincident(g3,g0)
    c: Horizontal(g2)
    c: Vertical(g1)
    c: Vertical(g3)
    c: PointOnObject(g1,g-1)
    c: DistanceY(g2,g0) = 22
    c: DistanceX(g0,g0) = 95
    c: Symmetric(g0,g0,g-2)
FEATURE [PartDesign::Plane] DatumPlane001 .. DatumPlane007  x7 (patterned run collapsed; names and placements below)
  AttachmentSupport = -> [Pad002]
  Length = 156.733
  MapMode = 5
  ResizeMode = 0
  Width = 66.7332
  placements: 7 in arithmetic series — first pos=(0,-62.9683,2.24e-14) rot=(1,0,0;1.5708rad), step (0,25.0317,-3.59e-14), last pos=(0,87.2216,0) rot=(1,0,0;1.5708rad)
FEATURE [PartDesign::Pocket] Pocket
  BaseFeature = -> Pad002
  Direction = (0,1,-2e-16)
  Length = 3.5
  Length2 = 5
  Profile = -> Sketch004
  ReferenceAxis = -> Sketch004 [N_Axis]
  Suppressed = false
  Type = 0
FEATURE [PartDesign::Pocket] Pocket001
  BaseFeature = -> Pocket
  Direction = (0,1,-2e-16)
  Length = 1
  Length2 = 5
  Profile = -> Sketch005
  ReferenceAxis = -> Sketch005 [N_Axis]
  Suppressed = false
  Type = 0
FEATURE [Sketcher::SketchObject] Sketch006
  ArcFitTolerance = 0
  AttachmentSupport = -> [DatumPlane001]
  FullyConstrained = true
  MakeInternals = false
  MapMode = 5
  Placement = pos=(0,-62.9683,2.24e-14) rot=(1,0,0;1.5708rad)
  expr: Constraints[38] = Sketch004.Constraints[38]
  expr: Constraints[39] = Sketch004.Constraints[39]
  expr: Constraints[40] = Sketch004.Constraints[40]
  sketch-geometry (14):
    g0: LineSegment StartX=-49.1979 StartY=11.775 StartZ=0 EndX=-49.1979 EndY=13.625 EndZ=0
    g1: LineSegment StartX=-49.1979 StartY=13.625 StartZ=0 EndX=-50.8 EndY=14.55 EndZ=0
    g2: LineSegment StartX=-50.8 StartY=14.55 StartZ=0 EndX=-52.4021 EndY=13.625 EndZ=0
    g3: LineSegment StartX=-52.4021 StartY=13.625 StartZ=0 EndX=-52.4021 EndY=11.775 EndZ=0
    g4: LineSegment StartX=-52.4021 StartY=11.775 StartZ=0 EndX=-50.8 EndY=10.85 EndZ=0
    g5: LineSegment StartX=-50.8 StartY=10.85 StartZ=0 EndX=-49.1979 EndY=11.775 EndZ=0
    g6: Circle [constr] CenterX=-50.8 CenterY=12.7 CenterZ=0 NormalX=0 NormalY=0 NormalZ=1 AngleXU=0 Radius=1.85
    g7: LineSegment StartX=52.4021 StartY=11.775 StartZ=0 EndX=52.4021 EndY=13.625 EndZ=0
    g8: LineSegment StartX=52.4021 StartY=13.625 StartZ=0 EndX=50.8 EndY=14.55 EndZ=0
    g9: LineSegment StartX=50.8 StartY=14.55 StartZ=0 EndX=49.1979 EndY=13.625 EndZ=0
    g10: LineSegment StartX=49.1979 StartY=13.625 StartZ=0 EndX=49.1979 EndY=11.775 EndZ=0
    g11: LineSegment StartX=49.1979 StartY=11.775 StartZ=0 EndX=50.8 EndY=10.85 EndZ=0
    g12: LineSegment StartX=50.8 StartY=10.85 StartZ=0 EndX=52.4021 EndY=11.775 EndZ=0
    g13: Circle [constr] CenterX=50.8 CenterY=12.7 CenterZ=0 NormalX=0 NormalY=0 NormalZ=1 AngleXU=0 Radius=1.85
  constraints (33):
    c: Coincident(g0,g1)
    c: Coincident(g1,g2)
    c: Coincident(g2,g3)
    c: Coincident(g3,g4)
    c: Coincident(g4,g5)
    c: Coincident(g5,g0)
    c: Equal(g0, g1-g5) x5
    c: PointOnObject(g0,g6)
    c: PointOnObject(g1,g6)
    c: PointOnObject(g2,g6)
    c: PointOnObject(g3,g6)
    c: PointOnObject(g4,g6)
    c: PointOnObject(g5,g6)
    c: Coincident(g7,g8)
    c: Coincident(g8,g9)
    c: Coincident(g9,g10)
    c: Coincident(g10,g11)
    c: Coincident(g11,g12)
    c: Coincident(g12,g7)
    c: Equal(g7, g8-g12) x5
    c: PointOnObject(g7,g13)
    c: PointOnObject(g8,g13)
    c: PointOnObject(g9,g13)
    c: PointOnObject(g10,g13)
    c: PointOnObject(g11,g13)
    c: PointOnObject(g12,g13)
    c: Parallel(g0,g-2)
    c: Equal(g2,g10)
    c: Parallel(g10,g-2)
    c: Symmetric(g6,g13,g-2)
    c: DistanceX(g6,g13) = 101.6
    c: DistanceY(g-1,g6) = 12.7
    c: Radius(g6) = 1.85
FEATURE [PartDesign::Pocket] Pocket002
  BaseFeature = -> Pocket001
  Direction = (0,1,-2e-16)
  Length = 3.5
  Length2 = 5
  Profile = -> Sketch006
  ReferenceAxis = -> Sketch006 [N_Axis]
  Suppressed = false
  Type = 0
FEATURE [Sketcher::SketchObject] Sketch007
  ArcFitTolerance = 0
  AttachmentSupport = -> [DatumPlane001]
  FullyConstrained = true
  MakeInternals = false
  MapMode = 5
  Placement = pos=(0,-62.9683,2.24e-14) rot=(1,0,0;1.5708rad)
  expr: Constraints[8] = Sketch005.Constraints[8]
  expr: Constraints[9] = Sketch005.Constraints[9]
  sketch-geometry (4):
    g0: LineSegment StartX=-47.5 StartY=22 StartZ=0 EndX=47.5 EndY=22 EndZ=0
    g1: LineSegment StartX=47.5 StartY=22 StartZ=0 EndX=47.5 EndY=0 EndZ=0
    g2: LineSegment StartX=47.5 StartY=0 StartZ=0 EndX=-47.5 EndY=0 EndZ=0
    g3: LineSegment StartX=-47.5 StartY=0 StartZ=0 EndX=-47.5 EndY=22 EndZ=0
  constraints (11):
    c: Coincident(g0,g1)
    c: Coincident(g1,g2)
    c: Coincident(g2,g3)
    c: Coincident(g3,g0)
    c: Horizontal(g2)
    c: Vertical(g1)
    c: Vertical(g3)
    c: PointOnObject(g1,g-1)
    c: DistanceY(g2,g0) = 22
    c: DistanceX(g0,g0) = 95
    c: Symmetric(g0,g0,g-2)
FEATURE [PartDesign::Pocket] Pocket003
  BaseFeature = -> Pocket002
  Direction = (0,1,-2e-16)
  Length = 1
  Length2 = 5
  Profile = -> Sketch007
  ReferenceAxis = -> Sketch007 [N_Axis]
  Suppressed = false
  Type = 0
FEATURE [Sketcher::SketchObject] Sketch008
  ArcFitTolerance = 0
  AttachmentSupport = -> [DatumPlane002]
  FullyConstrained = true
  MakeInternals = false
  MapMode = 5
  Placement = pos=(0,-37.9367,-1.35e-14) rot=(1,0,0;1.5708rad)
  expr: Constraints[38] = Sketch004.Constraints[38]
  expr: Constraints[39] = Sketch004.Constraints[39]
  expr: Constraints[40] = Sketch004.Constraints[40]
  sketch-geometry (14):
    g0: LineSegment StartX=-49.1979 StartY=11.775 StartZ=0 EndX=-49.1979 EndY=13.625 EndZ=0
    g1: LineSegment StartX=-49.1979 StartY=13.625 StartZ=0 EndX=-50.8 EndY=14.55 EndZ=0
    g2: LineSegment StartX=-50.8 StartY=14.55 StartZ=0 EndX=-52.4021 EndY=13.625 EndZ=0
    g3: LineSegment StartX=-52.4021 StartY=13.625 StartZ=0 EndX=-52.4021 EndY=11.775 EndZ=0
    g4: LineSegment StartX=-52.4021 StartY=11.775 StartZ=0 EndX=-50.8 EndY=10.85 EndZ=0
    g5: LineSegment StartX=-50.8 StartY=10.85 StartZ=0 EndX=-49.1979 EndY=11.775 EndZ=0
    g6: Circle [constr] CenterX=-50.8 CenterY=12.7 CenterZ=0 NormalX=0 NormalY=0 NormalZ=1 AngleXU=0 Radius=1.85
    g7: LineSegment StartX=52.4021 StartY=11.775 StartZ=0 EndX=52.4021 EndY=13.625 EndZ=0
    g8: LineSegment StartX=52.4021 StartY=13.625 StartZ=0 EndX=50.8 EndY=14.55 EndZ=0
    g9: LineSegment StartX=50.8 StartY=14.55 StartZ=0 EndX=49.1979 EndY=13.625 EndZ=0
    g10: LineSegment StartX=49.1979 StartY=13.625 StartZ=0 EndX=49.1979 EndY=11.775 EndZ=0
    g11: LineSegment StartX=49.1979 StartY=11.775 StartZ=0 EndX=50.8 EndY=10.85 EndZ=0
    g12: LineSegment StartX=50.8 StartY=10.85 StartZ=0 EndX=52.4021 EndY=11.775 EndZ=0
    g13: Circle [constr] CenterX=50.8 CenterY=12.7 CenterZ=0 NormalX=0 NormalY=0 NormalZ=1 AngleXU=0 Radius=1.85
  constraints (33):
    c: Coincident(g0,g1)
    c: Coincident(g1,g2)
    c: Coincident(g2,g3)
    c: Coincident(g3,g4)
    c: Coincident(g4,g5)
    c: Coincident(g5,g0)
    c: Equal(g0, g1-g5) x5
    c: PointOnObject(g0,g6)
    c: PointOnObject(g1,g6)
    c: PointOnObject(g2,g6)
    c: PointOnObject(g3,g6)
    c: PointOnObject(g4,g6)
    c: PointOnObject(g5,g6)
    c: Coincident(g7,g8)
    c: Coincident(g8,g9)
    c: Coincident(g9,g10)
    c: Coincident(g10,g11)
    c: Coincident(g11,g12)
    c: Coincident(g12,g7)
    c: Equal(g7, g8-g12) x5
    c: PointOnObject(g7,g13)
    c: PointOnObject(g8,g13)
    c: PointOnObject(g9,g13)
    c: PointOnObject(g10,g13)
    c: PointOnObject(g11,g13)
    c: PointOnObject(g12,g13)
    c: Parallel(g0,g-2)
    c: Equal(g2,g10)
    c: Parallel(g10,g-2)
    c: Symmetric(g6,g13,g-2)
    c: DistanceX(g6,g13) = 101.6
    c: DistanceY(g-1,g6) = 12.7
    c: Radius(g6) = 1.85
FEATURE [PartDesign::Pocket] Pocket004
  BaseFeature = -> Pocket003
  Direction = (0,1,-2e-16)
  Length = 3.5
  Length2 = 5
  Profile = -> Sketch008
  ReferenceAxis = -> Sketch008 [N_Axis]
  Suppressed = false
  Type = 0
FEATURE [Sketcher::SketchObject] Sketch009
  ArcFitTolerance = 0
  AttachmentSupport = -> [DatumPlane002]
  FullyConstrained = true
  MakeInternals = false
  MapMode = 5
  Placement = pos=(0,-37.9367,-1.35e-14) rot=(1,0,0;1.5708rad)
  expr: Constraints[8] = Sketch005.Constraints[8]
  expr: Constraints[9] = Sketch005.Constraints[9]
  sketch-geometry (4):
    g0: LineSegment StartX=-47.5 StartY=22 StartZ=0 EndX=47.5 EndY=22 EndZ=0
    g1: LineSegment StartX=47.5 StartY=22 StartZ=0 EndX=47.5 EndY=0 EndZ=0
    g2: LineSegment StartX=47.5 StartY=0 StartZ=0 EndX=-47.5 EndY=0 EndZ=0
    g3: LineSegment StartX=-47.5 StartY=0 StartZ=0 EndX=-47.5 EndY=22 EndZ=0
  constraints (11):
    c: Coincident(g0,g1)
    c: Coincident(g1,g2)
    c: Coincident(g2,g3)
    c: Coincident(g3,g0)
    c: Horizontal(g2)
    c: Vertical(g1)
    c: Vertical(g3)
    c: PointOnObject(g1,g-1)
    c: DistanceY(g2,g0) = 22
    c: DistanceX(g0,g0) = 95
    c: Symmetric(g0,g0,g-2)
FEATURE [PartDesign::Pocket] Pocket005
  BaseFeature = -> Pocket004
  Direction = (0,1,-2e-16)
  Length = 1
  Length2 = 5
  Profile = -> Sketch009
  ReferenceAxis = -> Sketch009 [N_Axis]
  Suppressed = false
  Type = 0
FEATURE [Sketcher::SketchObject] Sketch010
  ArcFitTolerance = 0
  AttachmentSupport = -> [DatumPlane003]
  FullyConstrained = true
  MakeInternals = false
  MapMode = 5
  Placement = pos=(0,-12.905,-3.4e-15) rot=(1,0,0;1.5708rad)
  expr: Constraints[38] = Sketch004.Constraints[38]
  expr: Constraints[39] = Sketch004.Constraints[39]
  expr: Constraints[40] = Sketch004.Constraints[40]
  sketch-geometry (14):
    g0: LineSegment StartX=-49.1979 StartY=11.775 StartZ=0 EndX=-49.1979 EndY=13.625 EndZ=0
    g1: LineSegment StartX=-49.1979 StartY=13.625 StartZ=0 EndX=-50.8 EndY=14.55 EndZ=0
    g2: LineSegment StartX=-50.8 StartY=14.55 StartZ=0 EndX=-52.4021 EndY=13.625 EndZ=0
    g3: LineSegment StartX=-52.4021 StartY=13.625 StartZ=0 EndX=-52.4021 EndY=11.775 EndZ=0
    g4: LineSegment StartX=-52.4021 StartY=11.775 StartZ=0 EndX=-50.8 EndY=10.85 EndZ=0
    g5: LineSegment StartX=-50.8 StartY=10.85 StartZ=0 EndX=-49.1979 EndY=11.775 EndZ=0
    g6: Circle [constr] CenterX=-50.8 CenterY=12.7 CenterZ=0 NormalX=0 NormalY=0 NormalZ=1 AngleXU=0 Radius=1.85
    g7: LineSegment StartX=52.4021 StartY=11.775 StartZ=0 EndX=52.4021 EndY=13.625 EndZ=0
    g8: LineSegment StartX=52.4021 StartY=13.625 StartZ=0 EndX=50.8 EndY=14.55 EndZ=0
    g9: LineSegment StartX=50.8 StartY=14.55 StartZ=0 EndX=49.1979 EndY=13.625 EndZ=0
    g10: LineSegment StartX=49.1979 StartY=13.625 StartZ=0 EndX=49.1979 EndY=11.775 EndZ=0
    g11: LineSegment StartX=49.1979 StartY=11.775 StartZ=0 EndX=50.8 EndY=10.85 EndZ=0
    g12: LineSegment StartX=50.8 StartY=10.85 StartZ=0 EndX=52.4021 EndY=11.775 EndZ=0
    g13: Circle [constr] CenterX=50.8 CenterY=12.7 CenterZ=0 NormalX=0 NormalY=0 NormalZ=1 AngleXU=0 Radius=1.85
  constraints (33):
    c: Coincident(g0,g1)
    c: Coincident(g1,g2)
    c: Coincident(g2,g3)
    c: Coincident(g3,g4)
    c: Coincident(g4,g5)
    c: Coincident(g5,g0)
    c: Equal(g0, g1-g5) x5
    c: PointOnObject(g0,g6)
    c: PointOnObject(g1,g6)
    c: PointOnObject(g2,g6)
    c: PointOnObject(g3,g6)
    c: PointOnObject(g4,g6)
    c: PointOnObject(g5,g6)
    c: Coincident(g7,g8)
    c: Coincident(g8,g9)
    c: Coincident(g9,g10)
    c: Coincident(g10,g11)
    c: Coincident(g11,g12)
    c: Coincident(g12,g7)
    c: Equal(g7, g8-g12) x5
    c: PointOnObject(g7,g13)
    c: PointOnObject(g8,g13)
    c: PointOnObject(g9,g13)
    c: PointOnObject(g10,g13)
    c: PointOnObject(g11,g13)
    c: PointOnObject(g12,g13)
    c: Parallel(g0,g-2)
    c: Equal(g2,g10)
    c: Parallel(g10,g-2)
    c: Symmetric(g6,g13,g-2)
    c: DistanceX(g6,g13) = 101.6
    c: DistanceY(g-1,g6) = 12.7
    c: Radius(g6) = 1.85
FEATURE [PartDesign::Pocket] Pocket006
  BaseFeature = -> Pocket005
  Direction = (0,1,-2e-16)
  Length = 3.5
  Length2 = 5
  Profile = -> Sketch010
  ReferenceAxis = -> Sketch010 [N_Axis]
  Suppressed = false
  Type = 0
FEATURE [Sketcher::SketchObject] Sketch011
  ArcFitTolerance = 0
  AttachmentSupport = -> [DatumPlane003]
  FullyConstrained = true
  MakeInternals = false
  MapMode = 5
  Placement = pos=(0,-12.905,-3.4e-15) rot=(1,0,0;1.5708rad)
  expr: Constraints[8] = Sketch005.Constraints[8]
  expr: Constraints[9] = Sketch005.Constraints[9]
  sketch-geometry (4):
    g0: LineSegment StartX=-47.5 StartY=22 StartZ=0 EndX=47.5 EndY=22 EndZ=0
    g1: LineSegment StartX=47.5 StartY=22 StartZ=0 EndX=47.5 EndY=0 EndZ=0
    g2: LineSegment StartX=47.5 StartY=0 StartZ=0 EndX=-47.5 EndY=0 EndZ=0
    g3: LineSegment StartX=-47.5 StartY=0 StartZ=0 EndX=-47.5 EndY=22 EndZ=0
  constraints (11):
    c: Coincident(g0,g1)
    c: Coincident(g1,g2)
    c: Coincident(g2,g3)
    c: Coincident(g3,g0)
    c: Horizontal(g2)
    c: Vertical(g1)
    c: Vertical(g3)
    c: PointOnObject(g1,g-1)
    c: DistanceY(g2,g0) = 22
    c: DistanceX(g0,g0) = 95
    c: Symmetric(g0,g0,g-2)
FEATURE [PartDesign::Pocket] Pocket007
  BaseFeature = -> Pocket006
  Direction = (0,1,-2e-16)
  Length = 1
  Length2 = 5
  Profile = -> Sketch011
  ReferenceAxis = -> Sketch011 [N_Axis]
  Suppressed = false
  Type = 0
FEATURE [Sketcher::SketchObject] Sketch012
  ArcFitTolerance = 0
  AttachmentSupport = -> [DatumPlane004]
  FullyConstrained = true
  MakeInternals = false
  MapMode = 5
  Placement = pos=(0,12.1266,2.2e-15) rot=(1,0,0;1.5708rad)
  expr: Constraints[38] = Sketch004.Constraints[38]
  expr: Constraints[39] = Sketch004.Constraints[39]
  expr: Constraints[40] = Sketch004.Constraints[40]
  sketch-geometry (14):
    g0: LineSegment StartX=-49.1979 StartY=11.775 StartZ=0 EndX=-49.1979 EndY=13.625 EndZ=0
    g1: LineSegment StartX=-49.1979 StartY=13.625 StartZ=0 EndX=-50.8 EndY=14.55 EndZ=0
    g2: LineSegment StartX=-50.8 StartY=14.55 StartZ=0 EndX=-52.4021 EndY=13.625 EndZ=0
    g3: LineSegment StartX=-52.4021 StartY=13.625 StartZ=0 EndX=-52.4021 EndY=11.775 EndZ=0
    g4: LineSegment StartX=-52.4021 StartY=11.775 StartZ=0 EndX=-50.8 EndY=10.85 EndZ=0
    g5: LineSegment StartX=-50.8 StartY=10.85 StartZ=0 EndX=-49.1979 EndY=11.775 EndZ=0
    g6: Circle [constr] CenterX=-50.8 CenterY=12.7 CenterZ=0 NormalX=0 NormalY=0 NormalZ=1 AngleXU=0 Radius=1.85
    g7: LineSegment StartX=52.4021 StartY=11.775 StartZ=0 EndX=52.4021 EndY=13.625 EndZ=0
    g8: LineSegment StartX=52.4021 StartY=13.625 StartZ=0 EndX=50.8 EndY=14.55 EndZ=0
    g9: LineSegment StartX=50.8 StartY=14.55 StartZ=0 EndX=49.1979 EndY=13.625 EndZ=0
    g10: LineSegment StartX=49.1979 StartY=13.625 StartZ=0 EndX=49.1979 EndY=11.775 EndZ=0
    g11: LineSegment StartX=49.1979 StartY=11.775 StartZ=0 EndX=50.8 EndY=10.85 EndZ=0
    g12: LineSegment StartX=50.8 StartY=10.85 StartZ=0 EndX=52.4021 EndY=11.775 EndZ=0
    g13: Circle [constr] CenterX=50.8 CenterY=12.7 CenterZ=0 NormalX=0 NormalY=0 NormalZ=1 AngleXU=0 Radius=1.85
  constraints (33):
    c: Coincident(g0,g1)
    c: Coincident(g1,g2)
    c: Coincident(g2,g3)
    c: Coincident(g3,g4)
    c: Coincident(g4,g5)
    c: Coincident(g5,g0)
    c: Equal(g0, g1-g5) x5
    c: PointOnObject(g0,g6)
    c: PointOnObject(g1,g6)
    c: PointOnObject(g2,g6)
    c: PointOnObject(g3,g6)
    c: PointOnObject(g4,g6)
    c: PointOnObject(g5,g6)
    c: Coincident(g7,g8)
    c: Coincident(g8,g9)
    c: Coincident(g9,g10)
    c: Coincident(g10,g11)
    c: Coincident(g11,g12)
    c: Coincident(g12,g7)
    c: Equal(g7, g8-g12) x5
    c: PointOnObject(g7,g13)
    c: PointOnObject(g8,g13)
    c: PointOnObject(g9,g13)
    c: PointOnObject(g10,g13)
    c: PointOnObject(g11,g13)
    c: PointOnObject(g12,g13)
    c: Parallel(g0,g-2)
    c: Equal(g2,g10)
    c: Parallel(g10,g-2)
    c: Symmetric(g6,g13,g-2)
    c: DistanceX(g6,g13) = 101.6
    c: DistanceY(g-1,g6) = 12.7
    c: Radius(g6) = 1.85
FEATURE [PartDesign::Pocket] Pocket008
  BaseFeature = -> Pocket007
  Direction = (0,1,-2e-16)
  Length = 3.5
  Length2 = 5
  Profile = -> Sketch012
  ReferenceAxis = -> Sketch012 [N_Axis]
  Suppressed = false
  Type = 0
FEATURE [Sketcher::SketchObject] Sketch013
  ArcFitTolerance = 0
  AttachmentSupport = -> [DatumPlane004]
  FullyConstrained = true
  MakeInternals = false
  MapMode = 5
  Placement = pos=(0,12.1266,2.2e-15) rot=(1,0,0;1.5708rad)
  expr: Constraints[8] = Sketch005.Constraints[8]
  expr: Constraints[9] = Sketch005.Constraints[9]
  sketch-geometry (4):
    g0: LineSegment StartX=-47.5 StartY=22 StartZ=0 EndX=47.5 EndY=22 EndZ=0
    g1: LineSegment StartX=47.5 StartY=22 StartZ=0 EndX=47.5 EndY=0 EndZ=0
    g2: LineSegment StartX=47.5 StartY=0 StartZ=0 EndX=-47.5 EndY=0 EndZ=0
    g3: LineSegment StartX=-47.5 StartY=0 StartZ=0 EndX=-47.5 EndY=22 EndZ=0
  constraints (11):
    c: Coincident(g0,g1)
    c: Coincident(g1,g2)
    c: Coincident(g2,g3)
    c: Coincident(g3,g0)
    c: Horizontal(g2)
    c: Vertical(g1)
    c: Vertical(g3)
    c: PointOnObject(g1,g-1)
    c: DistanceY(g2,g0) = 22
    c: DistanceX(g0,g0) = 95
    c: Symmetric(g0,g0,g-2)
FEATURE [PartDesign::Pocket] Pocket009
  BaseFeature = -> Pocket008
  Direction = (0,1,-2e-16)
  Length = 1
  Length2 = 5
  Profile = -> Sketch013
  ReferenceAxis = -> Sketch013 [N_Axis]
  Suppressed = false
  Type = 0
FEATURE [Sketcher::SketchObject] Sketch014
  ArcFitTolerance = 0
  AttachmentSupport = -> [DatumPlane005]
  FullyConstrained = true
  MakeInternals = false
  MapMode = 5
  Placement = pos=(0,37.1583,1.32e-14) rot=(1,0,0;1.5708rad)
  expr: Constraints[38] = Sketch004.Constraints[38]
  expr: Constraints[39] = Sketch004.Constraints[39]
  expr: Constraints[40] = Sketch004.Constraints[40]
  sketch-geometry (14):
    g0: LineSegment StartX=-49.1979 StartY=11.775 StartZ=0 EndX=-49.1979 EndY=13.625 EndZ=0
    g1: LineSegment StartX=-49.1979 StartY=13.625 StartZ=0 EndX=-50.8 EndY=14.55 EndZ=0
    g2: LineSegment StartX=-50.8 StartY=14.55 StartZ=0 EndX=-52.4021 EndY=13.625 EndZ=0
    g3: LineSegment StartX=-52.4021 StartY=13.625 StartZ=0 EndX=-52.4021 EndY=11.775 EndZ=0
    g4: LineSegment StartX=-52.4021 StartY=11.775 StartZ=0 EndX=-50.8 EndY=10.85 EndZ=0
    g5: LineSegment StartX=-50.8 StartY=10.85 StartZ=0 EndX=-49.1979 EndY=11.775 EndZ=0
    g6: Circle [constr] CenterX=-50.8 CenterY=12.7 CenterZ=0 NormalX=0 NormalY=0 NormalZ=1 AngleXU=0 Radius=1.85
    g7: LineSegment StartX=52.4021 StartY=11.775 StartZ=0 EndX=52.4021 EndY=13.625 EndZ=0
    g8: LineSegment StartX=52.4021 StartY=13.625 StartZ=0 EndX=50.8 EndY=14.55 EndZ=0
    g9: LineSegment StartX=50.8 StartY=14.55 StartZ=0 EndX=49.1979 EndY=13.625 EndZ=0
    g10: LineSegment StartX=49.1979 StartY=13.625 StartZ=0 EndX=49.1979 EndY=11.775 EndZ=0
    g11: LineSegment StartX=49.1979 StartY=11.775 StartZ=0 EndX=50.8 EndY=10.85 EndZ=0
    g12: LineSegment StartX=50.8 StartY=10.85 StartZ=0 EndX=52.4021 EndY=11.775 EndZ=0
    g13: Circle [constr] CenterX=50.8 CenterY=12.7 CenterZ=0 NormalX=0 NormalY=0 NormalZ=1 AngleXU=0 Radius=1.85
  constraints (33):
    c: Coincident(g0,g1)
    c: Coincident(g1,g2)
    c: Coincident(g2,g3)
    c: Coincident(g3,g4)
    c: Coincident(g4,g5)
    c: Coincident(g5,g0)
    c: Equal(g0, g1-g5) x5
    c: PointOnObject(g0,g6)
    c: PointOnObject(g1,g6)
    c: PointOnObject(g2,g6)
    c: PointOnObject(g3,g6)
    c: PointOnObject(g4,g6)
    c: PointOnObject(g5,g6)
    c: Coincident(g7,g8)
    c: Coincident(g8,g9)
    c: Coincident(g9,g10)
    c: Coincident(g10,g11)
    c: Coincident(g11,g12)
    c: Coincident(g12,g7)
    c: Equal(g7, g8-g12) x5
    c: PointOnObject(g7,g13)
    c: PointOnObject(g8,g13)
    c: PointOnObject(g9,g13)
    c: PointOnObject(g10,g13)
    c: PointOnObject(g11,g13)
    c: PointOnObject(g12,g13)
    c: Parallel(g0,g-2)
    c: Equal(g2,g10)
    c: Parallel(g10,g-2)
    c: Symmetric(g6,g13,g-2)
    c: DistanceX(g6,g13) = 101.6
    c: DistanceY(g-1,g6) = 12.7
    c: Radius(g6) = 1.85
FEATURE [PartDesign::Pocket] Pocket010
  BaseFeature = -> Pocket009
  Direction = (0,1,-2e-16)
  Length = 3.5
  Length2 = 5
  Profile = -> Sketch014
  ReferenceAxis = -> Sketch014 [N_Axis]
  Suppressed = false
  Type = 0
FEATURE [Sketcher::SketchObject] Sketch015
  ArcFitTolerance = 0
  AttachmentSupport = -> [DatumPlane005]
  FullyConstrained = true
  MakeInternals = false
  MapMode = 5
  Placement = pos=(0,37.1583,1.32e-14) rot=(1,0,0;1.5708rad)
  expr: Constraints[8] = Sketch005.Constraints[8]
  expr: Constraints[9] = Sketch005.Constraints[9]
  sketch-geometry (4):
    g0: LineSegment StartX=-47.5 StartY=22 StartZ=0 EndX=47.5 EndY=22 EndZ=0
    g1: LineSegment StartX=47.5 StartY=22 StartZ=0 EndX=47.5 EndY=0 EndZ=0
    g2: LineSegment StartX=47.5 StartY=0 StartZ=0 EndX=-47.5 EndY=0 EndZ=0
    g3: LineSegment StartX=-47.5 StartY=0 StartZ=0 EndX=-47.5 EndY=22 EndZ=0
  constraints (11):
    c: Coincident(g0,g1)
    c: Coincident(g1,g2)
    c: Coincident(g2,g3)
    c: Coincident(g3,g0)
    c: Horizontal(g2)
    c: Vertical(g1)
    c: Vertical(g3)
    c: PointOnObject(g1,g-1)
    c: DistanceY(g2,g0) = 22
    c: DistanceX(g0,g0) = 95
    c: Symmetric(g0,g0,g-2)
FEATURE [PartDesign::Pocket] Pocket011
  BaseFeature = -> Pocket010
  Direction = (0,1,-2e-16)
  Length = 1
  Length2 = 5
  Profile = -> Sketch015
  ReferenceAxis = -> Sketch015 [N_Axis]
  Suppressed = false
  Type = 0
FEATURE [Sketcher::SketchObject] Sketch016
  ArcFitTolerance = 0
  AttachmentSupport = -> [DatumPlane006]
  FullyConstrained = true
  MakeInternals = false
  MapMode = 5
  Placement = pos=(0,62.19,2.21e-14) rot=(1,0,0;1.5708rad)
  expr: Constraints[38] = Sketch004.Constraints[38]
  expr: Constraints[39] = Sketch004.Constraints[39]
  expr: Constraints[40] = Sketch004.Constraints[40]
  sketch-geometry (14):
    g0: LineSegment StartX=-49.1979 StartY=11.775 StartZ=0 EndX=-49.1979 EndY=13.625 EndZ=0
    g1: LineSegment StartX=-49.1979 StartY=13.625 StartZ=0 EndX=-50.8 EndY=14.55 EndZ=0
    g2: LineSegment StartX=-50.8 StartY=14.55 StartZ=0 EndX=-52.4021 EndY=13.625 EndZ=0
    g3: LineSegment StartX=-52.4021 StartY=13.625 StartZ=0 EndX=-52.4021 EndY=11.775 EndZ=0
    g4: LineSegment StartX=-52.4021 StartY=11.775 StartZ=0 EndX=-50.8 EndY=10.85 EndZ=0
    g5: LineSegment StartX=-50.8 StartY=10.85 StartZ=0 EndX=-49.1979 EndY=11.775 EndZ=0
    g6: Circle [constr] CenterX=-50.8 CenterY=12.7 CenterZ=0 NormalX=0 NormalY=0 NormalZ=1 AngleXU=0 Radius=1.85
    g7: LineSegment StartX=52.4021 StartY=11.775 StartZ=0 EndX=52.4021 EndY=13.625 EndZ=0
    g8: LineSegment StartX=52.4021 StartY=13.625 StartZ=0 EndX=50.8 EndY=14.55 EndZ=0
    g9: LineSegment StartX=50.8 StartY=14.55 StartZ=0 EndX=49.1979 EndY=13.625 EndZ=0
    g10: LineSegment StartX=49.1979 StartY=13.625 StartZ=0 EndX=49.1979 EndY=11.775 EndZ=0
    g11: LineSegment StartX=49.1979 StartY=11.775 StartZ=0 EndX=50.8 EndY=10.85 EndZ=0
    g12: LineSegment StartX=50.8 StartY=10.85 StartZ=0 EndX=52.4021 EndY=11.775 EndZ=0
    g13: Circle [constr] CenterX=50.8 CenterY=12.7 CenterZ=0 NormalX=0 NormalY=0 NormalZ=1 AngleXU=0 Radius=1.85
  constraints (33):
    c: Coincident(g0,g1)
    c: Coincident(g1,g2)
    c: Coincident(g2,g3)
    c: Coincident(g3,g4)
    c: Coincident(g4,g5)
    c: Coincident(g5,g0)
    c: Equal(g0, g1-g5) x5
    c: PointOnObject(g0,g6)
    c: PointOnObject(g1,g6)
    c: PointOnObject(g2,g6)
    c: PointOnObject(g3,g6)
    c: PointOnObject(g4,g6)
    c: PointOnObject(g5,g6)
    c: Coincident(g7,g8)
    c: Coincident(g8,g9)
    c: Coincident(g9,g10)
    c: Coincident(g10,g11)
    c: Coincident(g11,g12)
    c: Coincident(g12,g7)
    c: Equal(g7, g8-g12) x5
    c: PointOnObject(g7,g13)
    c: PointOnObject(g8,g13)
    c: PointOnObject(g9,g13)
    c: PointOnObject(g10,g13)
    c: PointOnObject(g11,g13)
    c: PointOnObject(g12,g13)
    c: Parallel(g0,g-2)
    c: Equal(g2,g10)
    c: Parallel(g10,g-2)
    c: Symmetric(g6,g13,g-2)
    c: DistanceX(g6,g13) = 101.6
    c: DistanceY(g-1,g6) = 12.7
    c: Radius(g6) = 1.85
FEATURE [PartDesign::Pocket] Pocket012
  BaseFeature = -> Pocket011
  Direction = (0,1,-2e-16)
  Length = 3.5
  Length2 = 5
  Profile = -> Sketch016
  ReferenceAxis = -> Sketch016 [N_Axis]
  Suppressed = false
  Type = 0
FEATURE [Sketcher::SketchObject] Sketch017
  ArcFitTolerance = 0
  AttachmentSupport = -> [DatumPlane006]
  FullyConstrained = true
  MakeInternals = false
  MapMode = 5
  Placement = pos=(0,62.19,2.21e-14) rot=(1,0,0;1.5708rad)
  expr: Constraints[8] = Sketch005.Constraints[8]
  expr: Constraints[9] = Sketch005.Constraints[9]
  sketch-geometry (4):
    g0: LineSegment StartX=-47.5 StartY=22 StartZ=0 EndX=47.5 EndY=22 EndZ=0
    g1: LineSegment StartX=47.5 StartY=22 StartZ=0 EndX=47.5 EndY=0 EndZ=0
    g2: LineSegment StartX=47.5 StartY=0 StartZ=0 EndX=-47.5 EndY=0 EndZ=0
    g3: LineSegment StartX=-47.5 StartY=0 StartZ=0 EndX=-47.5 EndY=22 EndZ=0
  constraints (11):
    c: Coincident(g0,g1)
    c: Coincident(g1,g2)
    c: Coincident(g2,g3)
    c: Coincident(g3,g0)
    c: Horizontal(g2)
    c: Vertical(g1)
    c: Vertical(g3)
    c: PointOnObject(g1,g-1)
    c: DistanceY(g2,g0) = 22
    c: DistanceX(g0,g0) = 95
    c: Symmetric(g0,g0,g-2)
FEATURE [PartDesign::Pocket] Pocket013
  BaseFeature = -> Pocket012
  Direction = (0,1,-2e-16)
  Length = 1
  Length2 = 5
  Profile = -> Sketch017
  ReferenceAxis = -> Sketch017 [N_Axis]
  Suppressed = false
  Type = 0
FEATURE [Sketcher::SketchObject] Sketch018
  ArcFitTolerance = 0
  AttachmentSupport = -> [DatumPlane007]
  FullyConstrained = true
  MakeInternals = false
  MapMode = 5
  Placement = pos=(0,87.2216,0) rot=(1,0,0;1.5708rad)
  expr: Constraints[38] = Sketch004.Constraints[38]
  expr: Constraints[39] = Sketch004.Constraints[39]
  expr: Constraints[40] = Sketch004.Constraints[40]
  sketch-geometry (14):
    g0: LineSegment StartX=-49.1979 StartY=11.775 StartZ=0 EndX=-49.1979 EndY=13.625 EndZ=0
    g1: LineSegment StartX=-49.1979 StartY=13.625 StartZ=0 EndX=-50.8 EndY=14.55 EndZ=0
    g2: LineSegment StartX=-50.8 StartY=14.55 StartZ=0 EndX=-52.4021 EndY=13.625 EndZ=0
    g3: LineSegment StartX=-52.4021 StartY=13.625 StartZ=0 EndX=-52.4021 EndY=11.775 EndZ=0
    g4: LineSegment StartX=-52.4021 StartY=11.775 StartZ=0 EndX=-50.8 EndY=10.85 EndZ=0
    g5: LineSegment StartX=-50.8 StartY=10.85 StartZ=0 EndX=-49.1979 EndY=11.775 EndZ=0
    g6: Circle [constr] CenterX=-50.8 CenterY=12.7 CenterZ=0 NormalX=0 NormalY=0 NormalZ=1 AngleXU=0 Radius=1.85
    g7: LineSegment StartX=52.4021 StartY=11.775 StartZ=0 EndX=52.4021 EndY=13.625 EndZ=0
    g8: LineSegment StartX=52.4021 StartY=13.625 StartZ=0 EndX=50.8 EndY=14.55 EndZ=0
    g9: LineSegment StartX=50.8 StartY=14.55 StartZ=0 EndX=49.1979 EndY=13.625 EndZ=0
    g10: LineSegment StartX=49.1979 StartY=13.625 StartZ=0 EndX=49.1979 EndY=11.775 EndZ=0
    g11: LineSegment StartX=49.1979 StartY=11.775 StartZ=0 EndX=50.8 EndY=10.85 EndZ=0
    g12: LineSegment StartX=50.8 StartY=10.85 StartZ=0 EndX=52.4021 EndY=11.775 EndZ=0
    g13: Circle [constr] CenterX=50.8 CenterY=12.7 CenterZ=0 NormalX=0 NormalY=0 NormalZ=1 AngleXU=0 Radius=1.85
  constraints (33):
    c: Coincident(g0,g1)
    c: Coincident(g1,g2)
    c: Coincident(g2,g3)
    c: Coincident(g3,g4)
    c: Coincident(g4,g5)
    c: Coincident(g5,g0)
    c: Equal(g0, g1-g5) x5
    c: PointOnObject(g0,g6)
    c: PointOnObject(g1,g6)
    c: PointOnObject(g2,g6)
    c: PointOnObject(g3,g6)
    c: PointOnObject(g4,g6)
    c: PointOnObject(g5,g6)
    c: Coincident(g7,g8)
    c: Coincident(g8,g9)
    c: Coincident(g9,g10)
    c: Coincident(g10,g11)
    c: Coincident(g11,g12)
    c: Coincident(g12,g7)
    c: Equal(g7, g8-g12) x5
    c: PointOnObject(g7,g13)
    c: PointOnObject(g8,g13)
    c: PointOnObject(g9,g13)
    c: PointOnObject(g10,g13)
    c: PointOnObject(g11,g13)
    c: PointOnObject(g12,g13)
    c: Parallel(g0,g-2)
    c: Equal(g2,g10)
    c: Parallel(g10,g-2)
    c: Symmetric(g6,g13,g-2)
    c: DistanceX(g6,g13) = 101.6
    c: DistanceY(g-1,g6) = 12.7
    c: Radius(g6) = 1.85
FEATURE [PartDesign::Pocket] Pocket014
  BaseFeature = -> Pocket013
  Direction = (0,1,-2e-16)
  Length = 3.5
  Length2 = 5
  Profile = -> Sketch018
  ReferenceAxis = -> Sketch018 [N_Axis]
  Suppressed = false
  Type = 0
FEATURE [Sketcher::SketchObject] Sketch019
  ArcFitTolerance = 0
  AttachmentSupport = -> [DatumPlane007]
  FullyConstrained = true
  MakeInternals = false
  MapMode = 5
  Placement = pos=(0,87.2216,0) rot=(1,0,0;1.5708rad)
  expr: Constraints[8] = Sketch005.Constraints[8]
  expr: Constraints[9] = Sketch005.Constraints[9]
  sketch-geometry (4):
    g0: LineSegment StartX=-47.5 StartY=22 StartZ=0 EndX=47.5 EndY=22 EndZ=0
    g1: LineSegment StartX=47.5 StartY=22 StartZ=0 EndX=47.5 EndY=0 EndZ=0
    g2: LineSegment StartX=47.5 StartY=0 StartZ=0 EndX=-47.5 EndY=0 EndZ=0
    g3: LineSegment StartX=-47.5 StartY=0 StartZ=0 EndX=-47.5 EndY=22 EndZ=0
  constraints (11):
    c: Coincident(g0,g1)
    c: Coincident(g1,g2)
    c: Coincident(g2,g3)
    c: Coincident(g3,g0)
    c: Horizontal(g2)
    c: Vertical(g1)
    c: Vertical(g3)
    c: PointOnObject(g1,g-1)
    c: DistanceY(g2,g0) = 22
    c: DistanceX(g0,g0) = 95
    c: Symmetric(g0,g0,g-2)
FEATURE [PartDesign::Pocket] Pocket015
  BaseFeature = -> Pocket014
  Direction = (0,1,-2e-16)
  Length = 1
  Length2 = 5
  Profile = -> Sketch019
  ReferenceAxis = -> Sketch019 [N_Axis]
  Suppressed = false
  Type = 0
FEATURE [Mesh::Feature] Mesh005  label="Body (Meshed)"
FEATURE [Sketcher::SketchObject] Sketch020
  ArcFitTolerance = 0
  AttachmentSupport = -> [XY_Plane]
  FullyConstrained = false
  MakeInternals = false
  MapMode = 5
  sketch-geometry (39):
    g0: LineSegment StartX=-47.5 StartY=80 StartZ=0 EndX=47.5 EndY=80 EndZ=0
    g1: LineSegment StartX=47.5 StartY=80 StartZ=0 EndX=47.5 EndY=72 EndZ=0
    g2: LineSegment StartX=47.5 StartY=72 StartZ=0 EndX=-47.5 EndY=72 EndZ=0
    g3: LineSegment StartX=-47.5 StartY=72 StartZ=0 EndX=-47.5 EndY=80 EndZ=0
    g4: LineSegment StartX=-47.5224 StartY=54.9462 StartZ=0 EndX=47.4776 EndY=54.9462 EndZ=0
    g5: LineSegment StartX=47.4776 StartY=54.9462 StartZ=0 EndX=47.4776 EndY=46.9462 EndZ=0
    g6: LineSegment StartX=47.4776 StartY=46.9462 StartZ=0 EndX=-47.5224 EndY=46.9462 EndZ=0
    g7: LineSegment StartX=-47.5224 StartY=46.9462 StartZ=0 EndX=-47.5224 EndY=54.9462 EndZ=0
    g8: LineSegment [constr] StartX=-47.5 StartY=80 StartZ=0 EndX=-47.5224 EndY=54.9462 EndZ=0
    g9: LineSegment StartX=-47.5448 StartY=29.8925 StartZ=0 EndX=47.4552 EndY=29.8925 EndZ=0
    g10: LineSegment StartX=47.4552 StartY=29.8925 StartZ=0 EndX=47.4552 EndY=21.8925 EndZ=0
    g11: LineSegment StartX=47.4552 StartY=21.8925 StartZ=0 EndX=-47.5448 EndY=21.8925 EndZ=0
    g12: LineSegment StartX=-47.5448 StartY=21.8925 StartZ=0 EndX=-47.5448 EndY=29.8925 EndZ=0
    g13: LineSegment [constr] StartX=-47.5224 StartY=54.9462 StartZ=0 EndX=-47.5448 EndY=29.8925 EndZ=0
    g14: LineSegment StartX=-47.5672 StartY=4.83868 StartZ=0 EndX=47.4328 EndY=4.83868 EndZ=0
    g15: LineSegment StartX=47.4328 StartY=4.83868 StartZ=0 EndX=47.4328 EndY=-3.16132 EndZ=0
    g16: LineSegment StartX=47.4328 StartY=-3.16132 StartZ=0 EndX=-47.5672 EndY=-3.16132 EndZ=0
    g17: LineSegment StartX=-47.5672 StartY=-3.16132 StartZ=0 EndX=-47.5672 EndY=4.83868 EndZ=0
    g18: LineSegment [constr] StartX=-47.5448 StartY=29.8925 StartZ=0 EndX=-47.5672 EndY=4.83868 EndZ=0
    g19: LineSegment StartX=-47.5896 StartY=-20.2151 StartZ=0 EndX=47.4104 EndY=-20.2151 EndZ=0
    g20: LineSegment StartX=47.4104 StartY=-20.2151 StartZ=0 EndX=47.4104 EndY=-28.2151 EndZ=0
    g21: LineSegment StartX=47.4104 StartY=-28.2151 StartZ=0 EndX=-47.5896 EndY=-28.2151 EndZ=0
    g22: LineSegment StartX=-47.5896 StartY=-28.2151 StartZ=0 EndX=-47.5896 EndY=-20.2151 EndZ=0
    g23: LineSegment [constr] StartX=-47.5672 StartY=4.83868 StartZ=0 EndX=-47.5896 EndY=-20.2151 EndZ=0
    g24: LineSegment StartX=-47.612 StartY=-45.2689 StartZ=0 EndX=47.388 EndY=-45.2689 EndZ=0
    g25: LineSegment StartX=47.388 StartY=-45.2689 StartZ=0 EndX=47.388 EndY=-53.2689 EndZ=0
    g26: LineSegment StartX=47.388 StartY=-53.2689 StartZ=0 EndX=-47.612 EndY=-53.2689 EndZ=0
    g27: LineSegment StartX=-47.612 StartY=-53.2689 StartZ=0 EndX=-47.612 EndY=-45.2689 EndZ=0
    g28: LineSegment [constr] StartX=-47.5896 StartY=-20.2151 StartZ=0 EndX=-47.612 EndY=-45.2689 EndZ=0
    g29: LineSegment StartX=-47.6344 StartY=-70.3226 StartZ=0 EndX=47.3656 EndY=-70.3226 EndZ=0
    g30: LineSegment StartX=47.3656 StartY=-70.3226 StartZ=0 EndX=47.3656 EndY=-78.3226 EndZ=0
    g31: LineSegment StartX=47.3656 StartY=-78.3226 StartZ=0 EndX=-47.6344 EndY=-78.3226 EndZ=0
    g32: LineSegment StartX=-47.6344 StartY=-78.3226 StartZ=0 EndX=-47.6344 EndY=-70.3226 EndZ=0
    g33: LineSegment [constr] StartX=-47.612 StartY=-45.2689 StartZ=0 EndX=-47.6344 EndY=-70.3226 EndZ=0
    g34: LineSegment StartX=-47.6569 StartY=-95.3764 StartZ=0 EndX=47.3431 EndY=-95.3764 EndZ=0
    g35: LineSegment StartX=47.3431 StartY=-95.3764 StartZ=0 EndX=47.3431 EndY=-103.376 EndZ=0
    g36: LineSegment StartX=47.3431 StartY=-103.376 StartZ=0 EndX=-47.6569 EndY=-103.376 EndZ=0
    g37: LineSegment StartX=-47.6569 StartY=-103.376 StartZ=0 EndX=-47.6569 EndY=-95.3764 EndZ=0
    g38: LineSegment [constr] StartX=-47.6344 StartY=-70.3226 StartZ=0 EndX=-47.6569 EndY=-95.3764 EndZ=0
  constraints (102):
    c: Coincident(g0,g1)
    c: Coincident(g1,g2)
    c: Coincident(g2,g3)
    c: Coincident(g3,g0)
    c: Horizontal(g2)
    c: Vertical(g1)
    c: Vertical(g3)
    c: Symmetric(g0,g0,g-2)
    c: DistanceX(g0,g0) = 95
    c: DistanceY(g2,g0) = 8
    c: DistanceY(g-1,g0) = 80
    c: Coincident(g4,g5)
    c: Coincident(g5,g6)
    c: Coincident(g6,g7)
    c: Coincident(g7,g4)
    c: Horizontal(g6)
    c: Vertical(g5)
    c: Vertical(g7)
    c: Equal(g0,g4) = 95
    c: DistanceY(g6,g4) = 8
    c: Coincident(g0,g8)
    c: Coincident(g4,g8)
    c: Distance(g8) = 25.0538
    c: Angle(g8) = -1.57169
    c: Coincident(g9,g10)
    c: Coincident(g10,g11)
    c: Coincident(g11,g12)
    c: Coincident(g12,g9)
    c: Horizontal(g11)
    c: Vertical(g10)
    c: Vertical(g12)
    c: Equal(g0,g9) = 95
    c: DistanceY(g11,g9) = 8
    c: Coincident(g4,g13)
    c: Coincident(g9,g13)
    c: Equal(g8,g13)
    c: Parallel(g13,g8)
    c: Coincident(g14,g15)
    c: Coincident(g15,g16)
    c: Coincident(g16,g17)
    c: Coincident(g17,g14)
    c: Horizontal(g16)
    c: Vertical(g15)
    c: Vertical(g17)
    c: Equal(g0,g14) = 95
    c: DistanceY(g16,g14) = 8
    c: Coincident(g9,g18)
    c: Coincident(g14,g18)
    c: Equal(g8,g18)
    c: Parallel(g18,g8)
    c: Coincident(g19,g20)
    c: Coincident(g20,g21)
    c: Coincident(g21,g22)
    c: Coincident(g22,g19)
    c: Horizontal(g21)
    c: Vertical(g20)
    c: Vertical(g22)
    c: Equal(g0,g19) = 95
    c: DistanceY(g21,g19) = 8
    c: Coincident(g14,g23)
    c: Coincident(g19,g23)
    c: Equal(g8,g23)
    c: Parallel(g23,g8)
    c: Coincident(g24,g25)
    c: Coincident(g25,g26)
    c: Coincident(g26,g27)
    c: Coincident(g27,g24)
    c: Horizontal(g26)
    c: Vertical(g25)
    c: Vertical(g27)
    c: Equal(g0,g24) = 95
    c: DistanceY(g26,g24) = 8
    c: Coincident(g19,g28)
    c: Coincident(g24,g28)
    c: Equal(g8,g28)
    c: Parallel(g28,g8)
    c: Coincident(g29,g30)
    c: Coincident(g30,g31)
    c: Coincident(g31,g32)
    c: Coincident(g32,g29)
    c: Horizontal(g31)
    c: Vertical(g30)
    c: Vertical(g32)
    c: Equal(g0,g29) = 95
    c: DistanceY(g31,g29) = 8
    c: Coincident(g24,g33)
    c: Coincident(g29,g33)
    c: Equal(g8,g33)
    c: Parallel(g33,g8)
    c: Coincident(g34,g35)
    c: Coincident(g35,g36)
    c: Coincident(g36,g37)
    c: Coincident(g37,g34)
    c: Horizontal(g36)
    c: Vertical(g35)
    c: Vertical(g37)
    c: Equal(g0,g34) = 95
    c: DistanceY(g36,g34) = 8
    c: Coincident(g29,g38)
    c: Coincident(g34,g38)
    c: Equal(g8,g38)
    c: Parallel(g38,g8)
FEATURE [PartDesign::Pocket] Pocket016
  BaseFeature = -> Pocket015
  Direction = (0,0,-1)
  Length = 10
  Length2 = -3
  Profile = -> Sketch020
  ReferenceAxis = -> Sketch020 [N_Axis]
  Reversed = true
  Suppressed = false
  Type = 4
FEATURE [PartDesign::Body] Body
  AllowCompound = false
  Group = -> [Sketch,Pad,Sketch001,Pad001,Sketch002,Pad002,DatumPlane,Sketch004,Sketch005,DatumPlane001,DatumPlane002,DatumPlane003,DatumPlane004,DatumPlane005,DatumPlane006,DatumPlane007,Pocket,Pocket001,Sketch006,Pocket002,Sketch007,Pocket003,Sketch008,Pocket004,Sketch009,Pocket005,Sketch010,Pocket006,Sketch011,Pocket007,Sketch012,Pocket008,Sketch013,Pocket009,Sketch014,Pocket010,Sketch015,Pocket011,+10 more]
  Origin = -> Origin
  Tip = -> Pocket016
